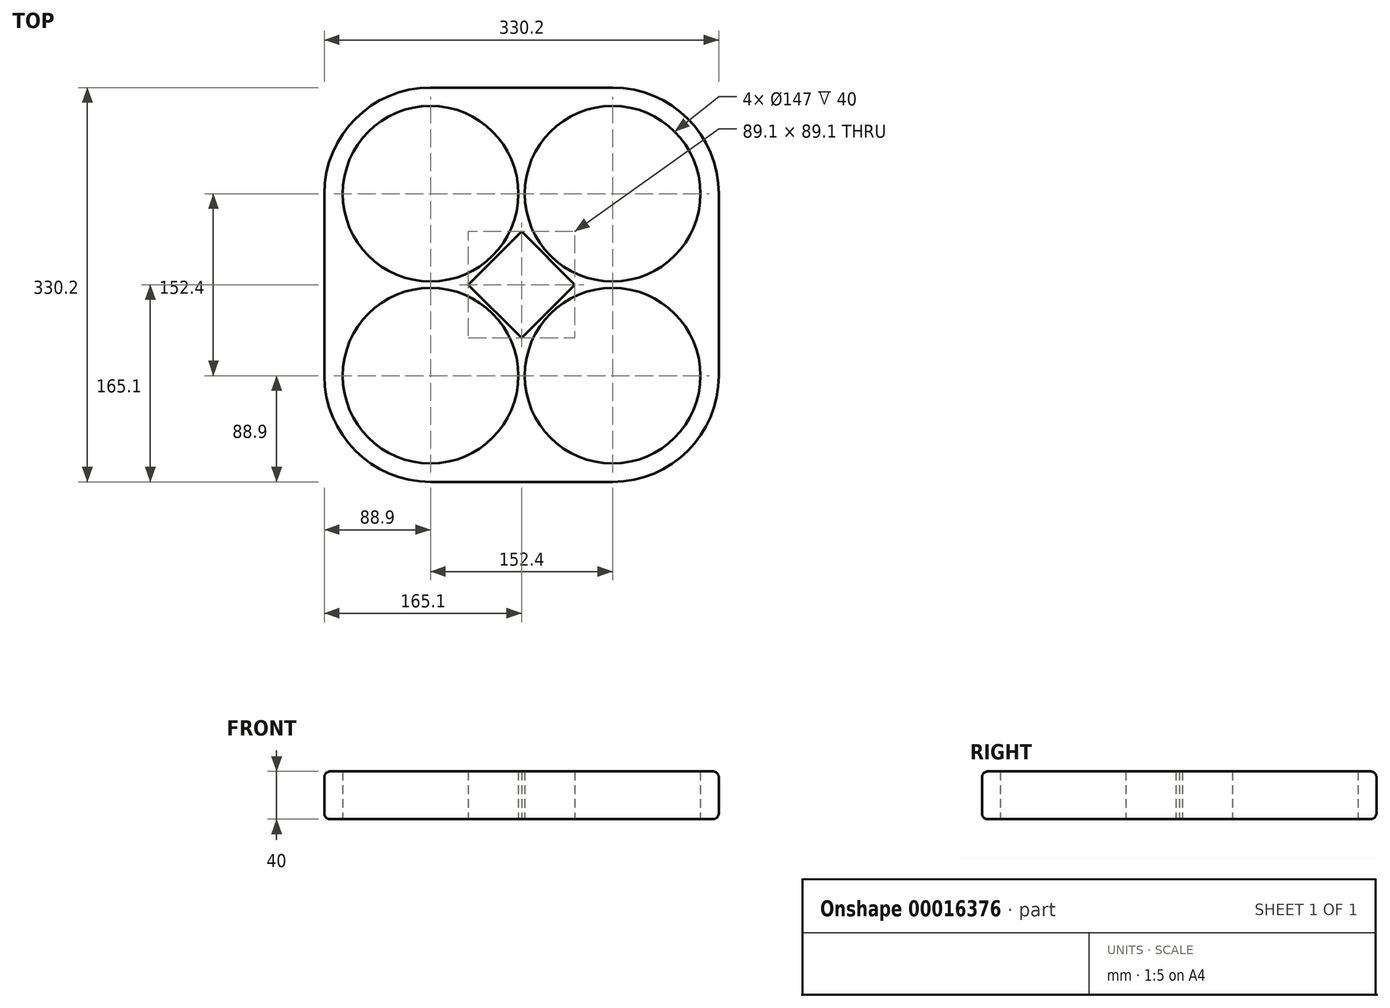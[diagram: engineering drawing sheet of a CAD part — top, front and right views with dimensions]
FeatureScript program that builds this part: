
annotation { "Feature Type Name" : "Feature", "Feature Type Description" : "" }
export const myFeature = defineFeature(function(context is Context, id is Id, definition is map)
    precondition{}
    {
        {
            var Q0;
            Q0=qCreatedBy(makeId("Top.planeOp"),FACE);
            var sketch = newSketch(context, id + "F0", { "sketchPlane" : qUnion([Q0])});
            skCircle(sketch, "E0", {"center": v(-76.2, 76.2) * mm, "radius": 73.5 * mm});
            skCircle(sketch, "E1", {"center": v(76.2, 76.2) * mm, "radius": 73.5 * mm});
            skCircle(sketch, "E2", {"center": v(76.2, -76.2) * mm, "radius": 73.5 * mm});
            skCircle(sketch, "E3", {"center": v(-76.2, -76.2) * mm, "radius": 73.5 * mm});
            skLineSegment(sketch, "E4", {"start": v(-76.2, 76.2) * mm, "end": v(76.2, 76.2) * mm, "construction": true});
            skLineSegment(sketch, "E5", {"start": v(76.2, -76.2) * mm, "end": v(76.2, 76.2) * mm, "construction": true});
            skLineSegment(sketch, "E6", {"start": v(-76.2, 76.2) * mm, "end": v(-76.2, -76.2) * mm, "construction": true});
            skLineSegment(sketch, "E7", {"start": v(-76.2, -76.2) * mm, "end": v(165.1, -76.2) * mm, "construction": true});
            skLineSegment(sketch, "E8.bottom", {"start": v(-76.2, 165.1) * mm, "end": v(76.2, 165.1) * mm});
            skLineSegment(sketch, "E8.top", {"start": v(-76.2, -165.1) * mm, "end": v(76.2, -165.1) * mm});
            skLineSegment(sketch, "E8.left", {"start": v(-165.1, 76.2) * mm, "end": v(-165.1, -76.2) * mm});
            skLineSegment(sketch, "E8.right", {"start": v(165.1, 76.2) * mm, "end": v(165.1, -76.2) * mm});
            skPoint(sketch, "E9.visualSharp", {"position": v(-165.1, 165.1) * mm});
            skArc(sketch, "E9.filletArc", {"start": v(-76.2, 165.1) * mm, "mid": v(-139.06, 139.06) * mm, "end": v(-165.1, 76.2) * mm});
            skPoint(sketch, "E10.visualSharp", {"position": v(165.1, 165.1) * mm});
            skArc(sketch, "E10.filletArc", {"start": v(165.1, 76.2) * mm, "mid": v(139.06, 139.06) * mm, "end": v(76.2, 165.1) * mm});
            skPoint(sketch, "E11.visualSharp", {"position": v(-165.1, -165.1) * mm});
            skArc(sketch, "E11.filletArc", {"start": v(-165.1, -76.2) * mm, "mid": v(-139.06, -139.06) * mm, "end": v(-76.2, -165.1) * mm});
            skPoint(sketch, "E12.visualSharp", {"position": v(165.1, -165.1) * mm});
            skArc(sketch, "E12.filletArc", {"start": v(76.2, -165.1) * mm, "mid": v(139.06, -139.06) * mm, "end": v(165.1, -76.2) * mm});
            skLineSegment(sketch, "E13", {"start": v(-44.55, 0) * mm, "end": v(0, 44.55) * mm});
            skLineSegment(sketch, "E14", {"start": v(0, 44.55) * mm, "end": v(44.55, 0) * mm});
            skLineSegment(sketch, "E15", {"start": v(44.55, 0) * mm, "end": v(0, -44.55) * mm});
            skLineSegment(sketch, "E16", {"start": v(0, -44.55) * mm, "end": v(-44.55, 0) * mm});
            skSolve(sketch);
        }
        {
            var Q0;
            Q0=qSketchRegion(id+"F0",true);
            extrude(context, id + "F1", {"entities" : qUnion([Q0]), "depth" : 40 * mm});
        }
        {
            var Q0;
            Q0=makeQuery(id+"F1.opExtrude","CAP_EDGE",EDGE,{"disambiguationData":[OSD([sQuery(id+"F0.wireOp",EDGE,"E11.filletArc")])],"isStart":false});
            fillet(context, id + "F2", {"entities" : qUnion([Q0]), "radius" : 5 * mm, "tangentPropagation" : true, "allowEdgeOverflow" : false});
        }
        {
            var Q0;
            Q0=makeQuery(id+"F1.opExtrude","CAP_EDGE",EDGE,{"disambiguationData":[OSD([sQuery(id+"F0.wireOp",EDGE,"E8.top")])],"isStart":true});
            fillet(context, id + "F3", {"entities" : qUnion([Q0]), "radius" : 5 * mm, "tangentPropagation" : true, "allowEdgeOverflow" : false});
        }
    });
